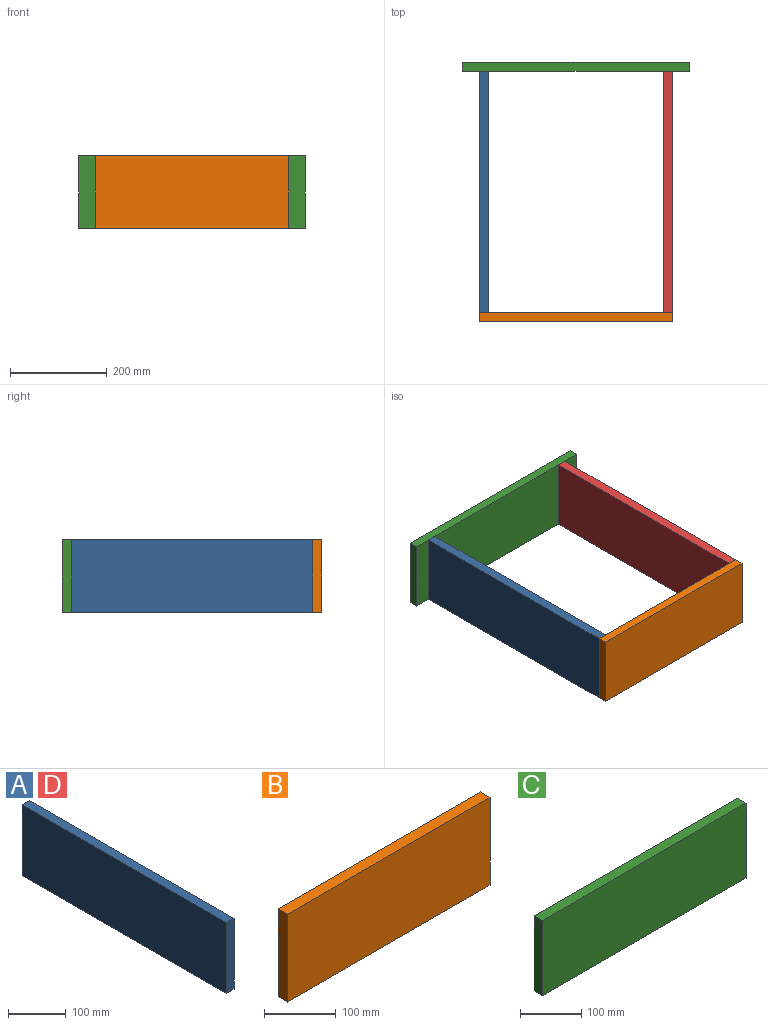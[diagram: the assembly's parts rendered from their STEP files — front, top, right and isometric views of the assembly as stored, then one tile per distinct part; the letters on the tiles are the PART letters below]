
ASSEMBLY  parts=4 mates=3
PART A: 6 faces, bbox 19x500x150 mm
  f0: plane 500x19mm, normal (0,0,1), area 9500mm2, adj f1,f3,f4,f5
  f1: plane 150x19mm, normal (0,-1,0), area 2850mm2, adj f0,f2,f4,f5
  f2: plane 500x19mm, normal (0,0,-1), area 9500mm2, adj f1,f3,f4,f5
  f3: plane 150x19mm, normal (0,1,0), area 2850mm2, adj f0,f2,f4,f5
  f4: plane 500x150mm, normal (1,0,0), area 75000mm2, adj f0,f1,f2,f3
  f5: plane 500x150mm, normal (-1,0,0), area 75000mm2, adj f0,f1,f2,f3
PART B: 6 faces, bbox 400x19x150 mm
  f0: plane 150x19mm, normal (1,0,0), area 2850mm2, adj f1,f3,f4,f5
  f1: plane 400x19mm, normal (0,0,1), area 7600mm2, adj f0,f2,f4,f5
  f2: plane 150x19mm, normal (-1,0,0), area 2850mm2, adj f1,f3,f4,f5
  f3: plane 400x19mm, normal (0,0,-1), area 7600mm2, adj f0,f2,f4,f5
  f4: plane 400x150mm, normal (0,-1,0), area 60000mm2, adj f0,f1,f2,f3
  f5: plane 400x150mm, normal (0,1,0), area 60000mm2, adj f0,f1,f2,f3
PART C: 6 faces, bbox 470x19x150 mm
  f0: plane 150x19mm, normal (1,0,0), area 2850mm2, adj f1,f3,f4,f5
  f1: plane 470x19mm, normal (0,0,1), area 8930mm2, adj f0,f2,f4,f5
  f2: plane 150x19mm, normal (-1,0,0), area 2850mm2, adj f1,f3,f4,f5
  f3: plane 470x19mm, normal (0,0,-1), area 8930mm2, adj f0,f2,f4,f5
  f4: plane 470x150mm, normal (0,-1,0), area 70500mm2, adj f0,f1,f2,f3
  f5: plane 470x150mm, normal (0,1,0), area 70500mm2, adj f0,f1,f2,f3
PART D: same geometry as A
PLACE A t=(-225.86,-239.55,52.32)mm
PLACE B t=(-25.86,-489.55,52.32)mm
PLACE C t=(-25.86,29.45,52.32)mm
PLACE D t=(155.14,-239.55,52.32)mm
MATE fastened A.f3 <-> C.f4  axis (0,1,0) through (-225.86,10.45,52.32)mm
MATE fastened B.f5 <-> D.f1  axis (0,1,0) through (174.14,-489.55,52.32)mm
MATE fastened D.f3 <-> C.f4  axis (0,1,0) through (174.14,10.45,52.32)mm
